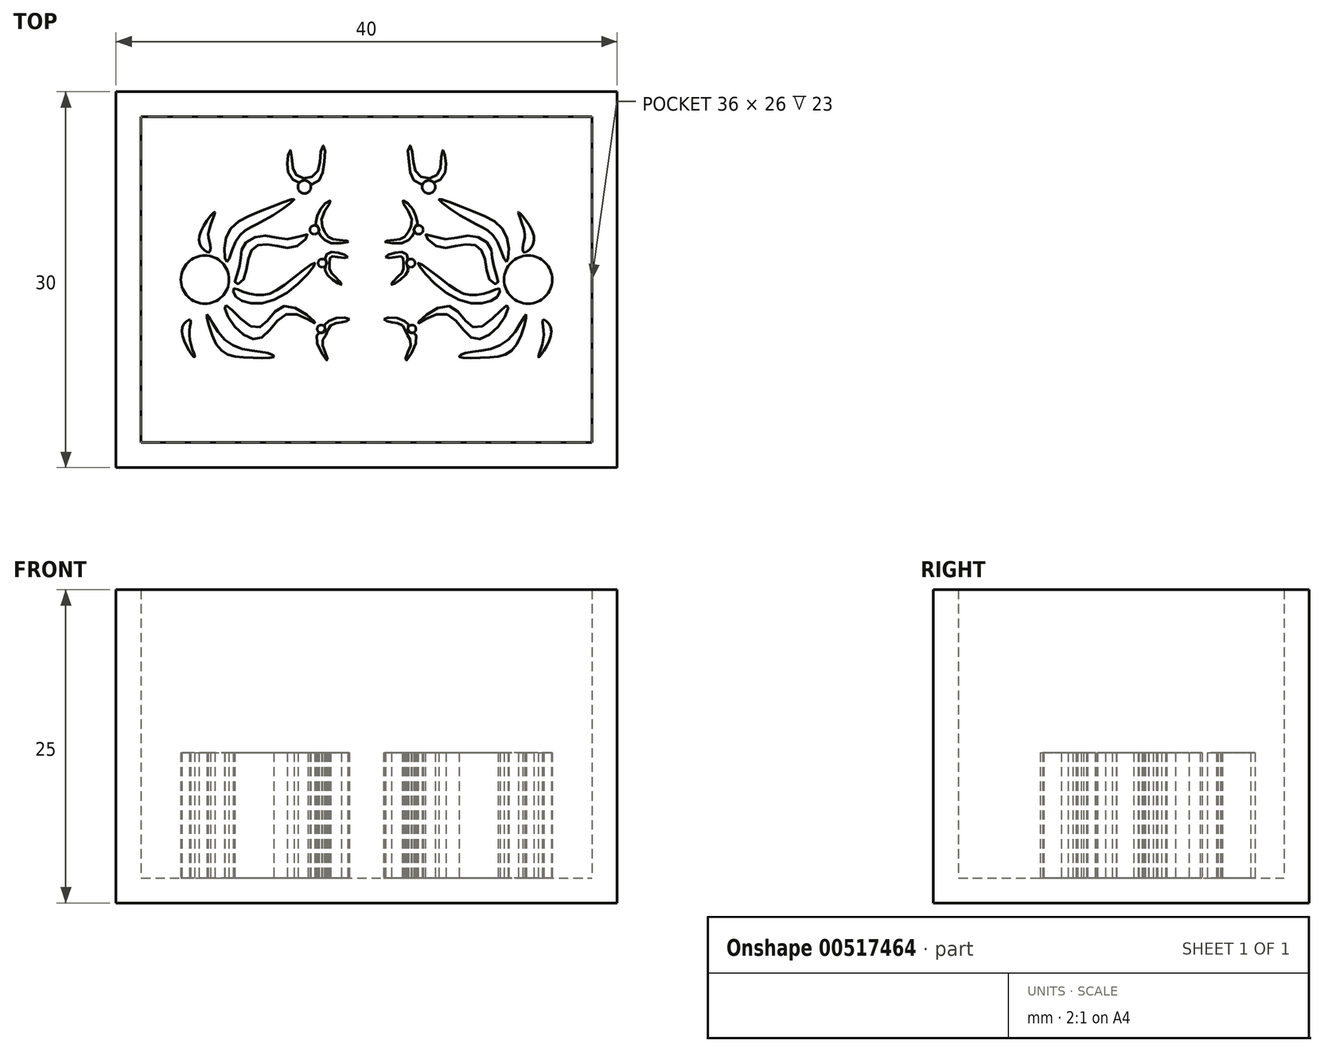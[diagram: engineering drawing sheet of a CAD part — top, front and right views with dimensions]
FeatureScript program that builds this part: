
annotation { "Feature Type Name" : "Feature", "Feature Type Description" : "" }
export const myFeature = defineFeature(function(context is Context, id is Id, definition is map)
    precondition{}
    {
        {
            var Q0;
            Q0=qCreatedBy(makeId("Top.planeOp"),FACE);
            var sketch = newSketch(context, id + "F0", { "sketchPlane" : qUnion([Q0])});
            skLineSegment(sketch, "E0.bottom", {"start": v(0, 0) * mm, "end": v(40, 0) * mm});
            skLineSegment(sketch, "E0.top", {"start": v(0, 30) * mm, "end": v(40, 30) * mm});
            skLineSegment(sketch, "E0.left", {"start": v(0, 0) * mm, "end": v(0, 30) * mm});
            skLineSegment(sketch, "E0.right", {"start": v(40, 0) * mm, "end": v(40, 30) * mm});
            skSolve(sketch);
        }
        {
            var Q0;
            Q0=makeQuery(id+"F0.imprint","IMPRINT",FACE,{"disambiguationData":[TD([[makeQuery(id+"F0.imprint","IMPRINT",EDGE,{"derivedFrom":sQuery(id+"F0.wireOp",EDGE,"E0.bottom")}),1.0]])]});
            extrude(context, id + "F1", {"entities" : qUnion([Q0]), "depth" : 25 * mm, "offsetDistance" : 25 * mm});
        }
        {
            var Q0;
            Q0=makeQuery(id+"F1.opExtrude","CAP_FACE",FACE,{"disambiguationData":[OSD([sQuery(id+"F0.wireOp",EDGE,"E0.bottom"),sQuery(id+"F0.wireOp",EDGE,"E0.top"),sQuery(id+"F0.wireOp",EDGE,"E0.left"),sQuery(id+"F0.wireOp",EDGE,"E0.right")])],"isStart":false});
            shell(context, id + "F2", {"entities" : qUnion([Q0]), "thickness" : 2 * mm});
        }
        {
            var Q0;
            Q0=makeQuery(id+"F2.opShell","OFFSET_FACE",FACE,{"disambiguationData":[OSD([sQuery(id+"F0.wireOp",EDGE,"E0.bottom"),sQuery(id+"F0.wireOp",EDGE,"E0.top"),sQuery(id+"F0.wireOp",EDGE,"E0.left"),sQuery(id+"F0.wireOp",EDGE,"E0.right")])]});
            var sketch = newSketch(context, id + "F3", { "sketchPlane" : qUnion([Q0])});
            skCircle(sketch, "E1", {"center": v(33.06, 17.38) * mm, "radius": 1.17 * mm});
            skSolve(sketch);
        }
        {
            var Q0;
            Q0 = qSketchRegion(id + "F3", true);
            extrude(context, id + "F4", {"entities" : qUnion([Q0]), "depth" : 10 * mm, "offsetDistance" : 25 * mm});
        }
        {
            var Q0;
            Q0=makeQuery(id+"F2.opShell","OFFSET_FACE",FACE,{"disambiguationData":[OSD([sQuery(id+"F0.wireOp",EDGE,"E0.bottom"),sQuery(id+"F0.wireOp",EDGE,"E0.top"),sQuery(id+"F0.wireOp",EDGE,"E0.left"),sQuery(id+"F0.wireOp",EDGE,"E0.right")])]});
            var sketch = newSketch(context, id + "F5", { "sketchPlane" : qUnion([Q0])});
            skCircle(sketch, "E2", {"center": v(34.3, 13.82) * mm, "radius": 1.1 * mm});
            skSolve(sketch);
        }
        {
            var Q0;
            Q0=makeQuery(id+"F5.imprint","IMPRINT",FACE,{"disambiguationData":[TD([[makeQuery(id+"F5.imprint","IMPRINT",EDGE,{"derivedFrom":sQuery(id+"F5.wireOp",EDGE,"E2")}),1.0]])]});
            extrude(context, id + "F6", {"entities" : qUnion([Q0]), "depth" : 10 * mm, "offsetDistance" : 25 * mm});
        }
        {
            var Q0;
            Q0=makeQuery(id+"F2.opShell","OFFSET_FACE",FACE,{"disambiguationData":[OSD([sQuery(id+"F0.wireOp",EDGE,"E0.bottom"),sQuery(id+"F0.wireOp",EDGE,"E0.top"),sQuery(id+"F0.wireOp",EDGE,"E0.left"),sQuery(id+"F0.wireOp",EDGE,"E0.right")])]});
            var sketch = newSketch(context, id + "F7", { "sketchPlane" : qUnion([Q0])});
            skCircle(sketch, "E3", {"center": v(21.96, 20.9) * mm, "radius": 2.86 * mm});
            skSolve(sketch);
        }
        {
            var Q0;
            Q0=makeQuery(id+"F7.imprint","IMPRINT",FACE,{"disambiguationData":[TD([[makeQuery(id+"F7.imprint","IMPRINT",EDGE,{"derivedFrom":sQuery(id+"F7.wireOp",EDGE,"E3")}),1.0]])]});
            extrude(context, id + "F8", {"entities" : qUnion([Q0]), "depth" : 25 * mm, "offsetDistance" : 25 * mm});
        }
        {
            var Q0;
            Q0=makeQuery(id+"F8.opExtrude","SWEPT_BODY",BODY,{"disambiguationData":[OSD([sQuery(id+"F7.wireOp",EDGE,"E3")])]});
            deleteBodies(context, id + "F9", {"entities" : qUnion([Q0])});
        }
        {
            var Q0;
            Q0=makeQuery(id+"F6.opExtrude","SWEPT_BODY",BODY,{"disambiguationData":[OSD([sQuery(id+"F5.wireOp",EDGE,"E2")])]});
            deleteBodies(context, id + "F10", {"entities" : qUnion([Q0])});
        }
        {
            var Q0;
            Q0=makeQuery(id+"F4.opExtrude","SWEPT_BODY",BODY,{"disambiguationData":[OSD([sQuery(id+"F3.wireOp",EDGE,"E1")])]});
            deleteBodies(context, id + "F11", {"entities" : qUnion([Q0])});
        }
        {
            var Q0;
            Q0=makeQuery(id+"F2.opShell","OFFSET_FACE",FACE,{"disambiguationData":[OSD([sQuery(id+"F0.wireOp",EDGE,"E0.bottom"),sQuery(id+"F0.wireOp",EDGE,"E0.top"),sQuery(id+"F0.wireOp",EDGE,"E0.left"),sQuery(id+"F0.wireOp",EDGE,"E0.right")])]});
            var sketch = newSketch(context, id + "F12", { "sketchPlane" : qUnion([Q0])});
            skCircle(sketch, "E4", {"center": v(32.9, 15) * mm, "radius": 1.92 * mm});
            skSolve(sketch);
        }
        {
            var Q0;
            Q0 = qSketchRegion(id + "F12", true);
            extrude(context, id + "F13", {"entities" : qUnion([Q0]), "depth" : 10 * mm, "offsetDistance" : 25 * mm});
        }
        {
            var Q0;
            Q0=qCreatedBy(makeId("Top.planeOp"),FACE);
            var sketch = newSketch(context, id + "F14", { "sketchPlane" : qUnion([Q0])});
            skCircle(sketch, "E5", {"center": v(32.77, 15.76) * mm, "radius": 0.71 * mm});
            skSolve(sketch);
        }
        {
            var Q0;
            Q0=sQuery(id+"F14.wireOp",EDGE,"E5");
            extrude(context, id + "F15", {"bodyType" : ToolBodyType.SURFACE, "surfaceEntities" : qUnion([Q0]), "depth" : 13 * mm, "offsetDistance" : 25 * mm});
        }
        {
            var Q0;
            Q0=qCreatedBy(makeId("Top.planeOp"),FACE);
            var sketch = newSketch(context, id + "F16", { "sketchPlane" : qUnion([Q0])});
            skCircle(sketch, "E6", {"center": v(33.33, 13.88) * mm, "radius": 0.58 * mm});
            skSolve(sketch);
        }
        {
            var Q0;
            Q0 = qSketchRegion(id + "F16", true);
            var Q1;
            Q1=sQuery(id+"F16.wireOp",EDGE,"E6");
            extrude(context, id + "F17", {"entities" : qUnion([Q0]), "bodyType" : ToolBodyType.SURFACE, "surfaceEntities" : qUnion([Q1]), "depth" : 13 * mm, "offsetDistance" : 25 * mm});
        }
        {
            var Q0;
            Q0=makeQuery(id+"F12.imprint","IMPRINT",FACE,{"disambiguationData":[TD([[makeQuery(id+"F12.imprint","IMPRINT",EDGE,{"derivedFrom":sQuery(id+"F12.wireOp",EDGE,"E4")}),-1.0]])]});
            var sketch = newSketch(context, id + "F18", { "sketchPlane" : qUnion([Q0])});
            skFitSpline(sketch, "E7", {"points": [v(31.16, 16.41) * mm, v(31.16, 18.52) * mm, v(28.04, 20.64) * mm, v(25.77, 21.42) * mm, v(27.7, 20) * mm, v(29.4, 19.1) * mm, v(30.5, 17.93) * mm, v(31.16, 16.41) * mm]});
            skSolve(sketch);
        }
        {
            var Q0;
            Q0 = qSketchRegion(id + "F18", true);
            extrude(context, id + "F19", {"entities" : qUnion([Q0]), "depth" : 10 * mm, "offsetDistance" : 25 * mm});
        }
        {
            var Q0;
            Q0=makeQuery(id+"F12.imprint","IMPRINT",FACE,{"disambiguationData":[TD([[makeQuery(id+"F12.imprint","IMPRINT",EDGE,{"derivedFrom":sQuery(id+"F12.wireOp",EDGE,"E4")}),-1.0]])]});
            var sketch = newSketch(context, id + "F20", { "sketchPlane" : qUnion([Q0])});
            skFitSpline(sketch, "E8", {"points": [v(33.17, 17.6) * mm, v(33.22, 18.88) * mm, v(32.12, 20.4) * mm, v(32.6, 18.84) * mm, v(32.48, 17.79) * mm, v(32.56, 17.17) * mm, v(33.17, 17.6) * mm]});
            skSolve(sketch);
        }
        {
            var Q0;
            Q0 = qSketchRegion(id + "F20", true);
            extrude(context, id + "F21", {"entities" : qUnion([Q0]), "depth" : 10 * mm, "offsetDistance" : 25 * mm});
        }
        {
            var Q0;
            Q0=makeQuery(id+"F12.imprint","IMPRINT",FACE,{"disambiguationData":[TD([[makeQuery(id+"F12.imprint","IMPRINT",EDGE,{"derivedFrom":sQuery(id+"F12.wireOp",EDGE,"E4")}),-1.0]])]});
            var sketch = newSketch(context, id + "F22", { "sketchPlane" : qUnion([Q0])});
            skFitSpline(sketch, "E9", {"points": [v(30.34, 15.44) * mm, v(30.04, 16.6) * mm, v(29.83, 17.7) * mm, v(28.31, 18.52) * mm, v(26.22, 18.24) * mm, v(24.69, 18.58) * mm, v(25.56, 17.68) * mm, v(27.24, 17.7) * mm, v(28.82, 17.68) * mm, v(29.46, 16.56) * mm, v(29.92, 14.87) * mm, v(30.47, 14.67) * mm, v(30.34, 15.44) * mm]});
            skSolve(sketch);
        }
        {
            var Q0;
            Q0 = qSketchRegion(id + "F22", true);
            extrude(context, id + "F23", {"entities" : qUnion([Q0]), "depth" : 10 * mm, "offsetDistance" : 25 * mm});
        }
        {
            var Q0;
            Q0=makeQuery(id+"F12.imprint","IMPRINT",FACE,{"disambiguationData":[TD([[makeQuery(id+"F12.imprint","IMPRINT",EDGE,{"derivedFrom":sQuery(id+"F12.wireOp",EDGE,"E4")}),-1.0]])]});
            var sketch = newSketch(context, id + "F24", { "sketchPlane" : qUnion([Q0])});
            skFitSpline(sketch, "E10", {"points": [v(30.43, 13.64) * mm, v(27.12, 13.5) * mm, v(24.13, 16.34) * mm, v(26.55, 14.6) * mm, v(28.42, 13.76) * mm, v(30.03, 14.1) * mm, v(30.6, 14.26) * mm, v(30.43, 13.64) * mm]});
            skSolve(sketch);
        }
        {
            var Q0;
            Q0 = qSketchRegion(id + "F24", true);
            extrude(context, id + "F25", {"entities" : qUnion([Q0]), "depth" : 10 * mm, "offsetDistance" : 25 * mm});
        }
        {
            var Q0;
            Q0=makeQuery(id+"F12.imprint","IMPRINT",FACE,{"disambiguationData":[TD([[makeQuery(id+"F12.imprint","IMPRINT",EDGE,{"derivedFrom":sQuery(id+"F12.wireOp",EDGE,"E4")}),-1.0]])]});
            var sketch = newSketch(context, id + "F26", { "sketchPlane" : qUnion([Q0])});
            skFitSpline(sketch, "E11", {"points": [v(31.2, 12.96) * mm, v(28.78, 11.15) * mm, v(26.48, 12.9) * mm, v(24.07, 11.51) * mm, v(26.19, 12.3) * mm, v(28.6, 10.27) * mm, v(31.02, 12) * mm, v(31.2, 12.96) * mm]});
            skSolve(sketch);
        }
        {
            var Q0;
            Q0 = qSketchRegion(id + "F26", true);
            extrude(context, id + "F27", {"entities" : qUnion([Q0]), "depth" : 10 * mm, "offsetDistance" : 25 * mm});
        }
        {
            var Q0;
            Q0=makeQuery(id+"F12.imprint","IMPRINT",FACE,{"disambiguationData":[TD([[makeQuery(id+"F12.imprint","IMPRINT",EDGE,{"derivedFrom":sQuery(id+"F12.wireOp",EDGE,"E4")}),-1.0]])]});
            var sketch = newSketch(context, id + "F28", { "sketchPlane" : qUnion([Q0])});
            skFitSpline(sketch, "E12", {"points": [v(32.73, 12.23) * mm, v(31.2, 10.1) * mm, v(27.93, 9.15) * mm, v(27.4, 8.85) * mm, v(29.68, 8.8) * mm, v(31.94, 9.76) * mm, v(32.73, 12.23) * mm]});
            skSolve(sketch);
        }
        {
            var Q0;
            Q0 = qSketchRegion(id + "F28", true);
            extrude(context, id + "F29", {"entities" : qUnion([Q0]), "depth" : 10 * mm, "offsetDistance" : 25 * mm});
        }
        {
            var Q0;
            Q0=makeQuery(id+"F12.imprint","IMPRINT",FACE,{"disambiguationData":[TD([[makeQuery(id+"F12.imprint","IMPRINT",EDGE,{"derivedFrom":sQuery(id+"F12.wireOp",EDGE,"E4")}),-1.0]])]});
            var sketch = newSketch(context, id + "F30", { "sketchPlane" : qUnion([Q0])});
            skFitSpline(sketch, "E13", {"points": [v(34.08, 11.79) * mm, v(34.75, 11) * mm, v(33.74, 8.83) * mm, v(34.14, 10.5) * mm, v(34.08, 11.79) * mm]});
            skSolve(sketch);
        }
        {
            var Q0;
            Q0 = qSketchRegion(id + "F30", true);
            extrude(context, id + "F31", {"entities" : qUnion([Q0]), "depth" : 10 * mm, "offsetDistance" : 25 * mm});
        }
        {
            var Q0;
            Q0=qCreatedBy(makeId("Right.planeOp"),FACE);
            cPlane(context, id + "F32", {"entities" : qUnion([Q0]), "cplaneType" : CPlaneType.OFFSET, "offset" : 20 * mm, "width" : 150 * mm, "height" : 150 * mm});
        }
        {
            var Q0;
            Q0=makeQuery(id+"F12.imprint","IMPRINT",FACE,{"disambiguationData":[TD([[makeQuery(id+"F12.imprint","IMPRINT",EDGE,{"derivedFrom":sQuery(id+"F12.wireOp",EDGE,"E4")}),-1.0]])]});
            var sketch = newSketch(context, id + "F33", { "sketchPlane" : qUnion([Q0])});
            skCircle(sketch, "E14", {"center": v(25.04, 22.1) * mm, "radius": 0.48 * mm});
            skFitSpline(sketch, "E15", {"points": [v(24.78, 21.7) * mm, v(24.43, 20.97) * mm, v(22.2, 21.2) * mm, v(21.84, 21.56) * mm, v(22.86, 21.49) * mm, v(23.88, 21.52) * mm, v(24.03, 22.1) * mm, v(24.25, 22.94) * mm, v(23.92, 23.98) * mm, v(23.94, 24.53) * mm, v(24.5, 24.08) * mm, v(25.04, 22.58) * mm], "startDerivative": vector(-1.18, -10.43) * mm, "endDerivative": vector(3.27, -13.82) * mm});
            skSolve(sketch);
        }
        {
            var Q0;
            Q0 = qSketchRegion(id + "F33", true);
            extrude(context, id + "F34", {"entities" : qUnion([Q0]), "depth" : 10 * mm, "offsetDistance" : 25 * mm});
        }
        {
            var Q0;
            Q0=makeQuery(id+"F12.imprint","IMPRINT",FACE,{"disambiguationData":[TD([[makeQuery(id+"F12.imprint","IMPRINT",EDGE,{"derivedFrom":sQuery(id+"F12.wireOp",EDGE,"E4")}),-1.0]])]});
            var sketch = newSketch(context, id + "F35", { "sketchPlane" : qUnion([Q0])});
            skCircle(sketch, "E16", {"center": v(23.7, 18.69) * mm, "radius": 0.52 * mm});
            skFitSpline(sketch, "E17", {"points": [v(23.7, 18.17) * mm, v(22.99, 17.37) * mm, v(21.27, 16.99) * mm, v(22.58, 17.78) * mm, v(22.88, 18.1) * mm, v(22.76, 18.69) * mm, v(22.73, 19.4) * mm, v(22.13, 20.23) * mm, v(22, 20.54) * mm, v(22.5, 20.52) * mm, v(23.14, 19.83) * mm, v(23.2, 19.49) * mm, v(23.34, 19.05) * mm], "startDerivative": vector(-4, -8.51) * mm, "endDerivative": vector(2.63, -7.06) * mm});
            skSolve(sketch);
        }
        {
            var Q0;
            Q0 = qSketchRegion(id + "F35", true);
            extrude(context, id + "F36", {"entities" : qUnion([Q0]), "depth" : 10 * mm, "offsetDistance" : 25 * mm});
        }
        {
            var Q0;
            Q0=makeQuery(id+"F12.imprint","IMPRINT",FACE,{"disambiguationData":[TD([[makeQuery(id+"F12.imprint","IMPRINT",EDGE,{"derivedFrom":sQuery(id+"F12.wireOp",EDGE,"E4")}),-1.0]])]});
            var sketch = newSketch(context, id + "F37", { "sketchPlane" : qUnion([Q0])});
            skCircle(sketch, "E18", {"center": v(23.12, 15.63) * mm, "radius": 0.5 * mm});
            skFitSpline(sketch, "E19", {"points": [v(22.97, 16.1) * mm, v(22.2, 16.43) * mm, v(20.6, 16.07) * mm, v(20.43, 15.68) * mm, v(21.42, 15.94) * mm, v(22.63, 15.73) * mm, v(22.28, 14.57) * mm, v(21.91, 13.4) * mm, v(22.77, 14.04) * mm, v(23.12, 15.13) * mm], "startDerivative": vector(-6.4, 4.26) * mm, "endDerivative": vector(1.17, 9.37) * mm});
            skSolve(sketch);
        }
        {
            var Q0;
            Q0 = qSketchRegion(id + "F37", true);
            extrude(context, id + "F38", {"entities" : qUnion([Q0]), "depth" : 10 * mm, "offsetDistance" : 25 * mm});
        }
        {
            var Q0;
            Q0=makeQuery(id+"F12.imprint","IMPRINT",FACE,{"disambiguationData":[TD([[makeQuery(id+"F12.imprint","IMPRINT",EDGE,{"derivedFrom":sQuery(id+"F12.wireOp",EDGE,"E4")}),-1.0]])]});
            var sketch = newSketch(context, id + "F39", { "sketchPlane" : qUnion([Q0])});
            skCircle(sketch, "E20", {"center": v(23.48, 10.89) * mm, "radius": 0.36 * mm});
            skFitSpline(sketch, "E21", {"points": [v(23.8, 10.7) * mm, v(24.59, 9.36) * mm, v(23.9, 7.91) * mm, v(24.05, 8.75) * mm, v(24.07, 9.56) * mm, v(23.4, 10.23) * mm, v(22.57, 10.68) * mm, v(21.36, 10.65) * mm, v(20.96, 10.76) * mm, v(21.98, 11.04) * mm, v(23.13, 10.99) * mm], "startDerivative": vector(10.24, -8.94) * mm, "endDerivative": vector(9.79, -1.38) * mm});
            skSolve(sketch);
        }
        {
            var Q0;
            Q0 = qSketchRegion(id + "F39", true);
            extrude(context, id + "F40", {"entities" : qUnion([Q0]), "depth" : 10 * mm, "offsetDistance" : 25 * mm});
        }
        {
            var Q0;
            Q0=makeQuery(id+"F34.opExtrude","SWEPT_BODY",BODY,{"disambiguationData":[OSD([sQuery(id+"F33.wireOp",EDGE,"E14"),sQuery(id+"F33.wireOp",EDGE,"E15")])]});
            deleteBodies(context, id + "F41", {"entities" : qUnion([Q0])});
        }
        {
            var Q0;
            Q0=makeQuery(id+"F12.imprint","IMPRINT",FACE,{"disambiguationData":[TD([[makeQuery(id+"F12.imprint","IMPRINT",EDGE,{"derivedFrom":sQuery(id+"F12.wireOp",EDGE,"E4")}),-1.0]])]});
            var sketch = newSketch(context, id + "F42", { "sketchPlane" : qUnion([Q0])});
            skCircle(sketch, "E22", {"center": v(24.96, 22.4) * mm, "radius": 0.52 * mm});
            skSolve(sketch);
        }
        {
            var Q0;
            Q0 = qSketchRegion(id + "F42", true);
            extrude(context, id + "F43", {"entities" : qUnion([Q0]), "depth" : 10 * mm, "offsetDistance" : 25 * mm});
        }
        {
            var Q0;
            Q0=makeQuery(id+"F42.imprint","IMPRINT",FACE,{"disambiguationData":[TD([[makeQuery(id+"F42.imprint","IMPRINT",EDGE,{"derivedFrom":sQuery(id+"F42.wireOp",EDGE,"E22")}),-1.0]])]});
            var sketch = newSketch(context, id + "F44", { "sketchPlane" : qUnion([Q0])});
            skFitSpline(sketch, "E23", {"points": [v(25.37, 22.74) * mm, v(26.07, 23.17) * mm, v(26.34, 24.1) * mm, v(26.22, 25.08) * mm, v(26.07, 25.33) * mm, v(25.94, 24.28) * mm, v(25.63, 23.36) * mm, v(24.72, 23.09) * mm, v(23.93, 23.63) * mm, v(23.7, 24.8) * mm, v(23.5, 25.69) * mm, v(23.34, 25.56) * mm, v(23.42, 24.1) * mm, v(23.74, 22.96) * mm, v(24.46, 22.6) * mm, v(24.5, 22.66) * mm, v(24.62, 22.8) * mm, v(24.8, 22.91) * mm, v(25.01, 22.94) * mm, v(25.22, 22.88) * mm, v(25.37, 22.74) * mm]});
            skSolve(sketch);
        }
        {
            var Q0;
            Q0 = qSketchRegion(id + "F44", true);
            extrude(context, id + "F45", {"entities" : qUnion([Q0]), "depth" : 10 * mm, "offsetDistance" : 25 * mm});
        }
        {
            var Q0;
            Q0=makeQuery(id+"F36.opExtrude","SWEPT_BODY",BODY,{"disambiguationData":[OSD([sQuery(id+"F35.wireOp",EDGE,"E16"),sQuery(id+"F35.wireOp",EDGE,"E17")])]});
            deleteBodies(context, id + "F46", {"entities" : qUnion([Q0])});
        }
        {
            var Q0;
            Q0=makeQuery(id+"F12.imprint","IMPRINT",FACE,{"disambiguationData":[TD([[makeQuery(id+"F12.imprint","IMPRINT",EDGE,{"derivedFrom":sQuery(id+"F12.wireOp",EDGE,"E4")}),-1.0]])]});
            var sketch = newSketch(context, id + "F47", { "sketchPlane" : qUnion([Q0])});
            skCircle(sketch, "E24", {"center": v(24.17, 18.98) * mm, "radius": 0.35 * mm});
            skSolve(sketch);
        }
        {
            var Q0;
            Q0 = qSketchRegion(id + "F47", true);
            extrude(context, id + "F48", {"entities" : qUnion([Q0]), "depth" : 10 * mm, "offsetDistance" : 25 * mm});
        }
        {
            var Q0;
            Q0=makeQuery(id+"F12.imprint","IMPRINT",FACE,{"disambiguationData":[TD([[makeQuery(id+"F12.imprint","IMPRINT",EDGE,{"derivedFrom":sQuery(id+"F12.wireOp",EDGE,"E4")}),-1.0]])]});
            var sketch = newSketch(context, id + "F49", { "sketchPlane" : qUnion([Q0])});
            skFitSpline(sketch, "E25", {"points": [v(23.82, 18.85) * mm, v(23.8, 19.02) * mm, v(23.86, 19.18) * mm, v(24.02, 19.31) * mm, v(24.22, 19.34) * mm, v(24.58, 19.5) * mm, v(24.83, 20.22) * mm, v(24.83, 20.8) * mm, v(24.74, 21.12) * mm, v(24.6, 20.81) * mm, v(24.49, 20) * mm, v(24.02, 19.63) * mm, v(23.18, 19.78) * mm, v(22.71, 20.6) * mm, v(22.59, 20.88) * mm, v(22.5, 20.72) * mm, v(22.81, 19.85) * mm, v(23.39, 19.17) * mm, v(23.6, 19.04) * mm, v(23.82, 18.85) * mm]});
            skSolve(sketch);
        }
        {
            var Q0;
            Q0 = qSketchRegion(id + "F49", true);
            extrude(context, id + "F50", {"entities" : qUnion([Q0]), "depth" : 10 * mm, "offsetDistance" : 25 * mm});
        }
        {
            var Q0;
            Q0=makeQuery(id+"F50.opExtrude","SWEPT_BODY",BODY,{"disambiguationData":[OSD([sQuery(id+"F49.wireOp",EDGE,"E25")])]});
            deleteBodies(context, id + "F51", {"entities" : qUnion([Q0])});
        }
        {
            var Q0;
            Q0=makeQuery(id+"F42.imprint","IMPRINT",FACE,{"disambiguationData":[TD([[makeQuery(id+"F42.imprint","IMPRINT",EDGE,{"derivedFrom":sQuery(id+"F42.wireOp",EDGE,"E22")}),-1.0]])]});
            var sketch = newSketch(context, id + "F52", { "sketchPlane" : qUnion([Q0])});
            skFitSpline(sketch, "E26", {"points": [v(24.04, 19.34) * mm, v(24.27, 19.37) * mm, v(24.84, 19.6) * mm, v(24.76, 20.82) * mm, v(24.42, 21.37) * mm, v(24.58, 20.37) * mm, v(24.59, 19.9) * mm, v(23.82, 19.7) * mm, v(22.97, 20.08) * mm, v(22.37, 20.98) * mm, v(22, 20.98) * mm, v(22.74, 19.95) * mm, v(23.42, 19.37) * mm, v(23.8, 19.22) * mm, v(24.04, 19.34) * mm]});
            skSolve(sketch);
        }
        {
            var Q0;
            Q0 = qSketchRegion(id + "F52", true);
            extrude(context, id + "F53", {"entities" : qUnion([Q0]), "depth" : 10 * mm, "offsetDistance" : 25 * mm});
        }
        {
            var Q0;
            Q0=makeQuery(id+"F38.opExtrude","SWEPT_BODY",BODY,{"disambiguationData":[OSD([sQuery(id+"F37.wireOp",EDGE,"E18"),sQuery(id+"F37.wireOp",EDGE,"E19")])]});
            deleteBodies(context, id + "F54", {"entities" : qUnion([Q0])});
        }
        {
            var Q0;
            Q0=makeQuery(id+"F53.opExtrude","SWEPT_BODY",BODY,{"disambiguationData":[OSD([sQuery(id+"F52.wireOp",EDGE,"E26")])]});
            deleteBodies(context, id + "F55", {"entities" : qUnion([Q0])});
        }
        {
            var Q0;
            Q0=makeQuery(id+"F12.imprint","IMPRINT",FACE,{"disambiguationData":[TD([[makeQuery(id+"F12.imprint","IMPRINT",EDGE,{"derivedFrom":sQuery(id+"F12.wireOp",EDGE,"E4")}),-1.0]])]});
            var sketch = newSketch(context, id + "F56", { "sketchPlane" : qUnion([Q0])});
            skFitSpline(sketch, "E27", {"points": [v(23.78, 19) * mm, v(23.81, 18.8) * mm, v(23.65, 18.49) * mm, v(22.87, 17.94) * mm, v(21.44, 18.03) * mm, v(22.03, 18.16) * mm, v(22.92, 18.33) * mm, v(23.4, 18.92) * mm, v(23.54, 20.06) * mm, v(22.85, 21.28) * mm, v(23.4, 21.01) * mm, v(24, 19.86) * mm, v(24.08, 19.4) * mm, v(24.05, 19.35) * mm, v(23.93, 19.29) * mm, v(23.78, 19) * mm]});
            skSolve(sketch);
        }
        {
            var Q0;
            Q0 = qSketchRegion(id + "F56", true);
            extrude(context, id + "F57", {"entities" : qUnion([Q0]), "depth" : 10 * mm, "offsetDistance" : 25 * mm});
        }
        {
            var Q0;
            Q0=makeQuery(id+"F40.opExtrude","SWEPT_BODY",BODY,{"disambiguationData":[OSD([sQuery(id+"F39.wireOp",EDGE,"E20"),sQuery(id+"F39.wireOp",EDGE,"E21")])]});
            deleteBodies(context, id + "F58", {"entities" : qUnion([Q0])});
        }
        {
            var Q0;
            Q0=makeQuery(id+"F12.imprint","IMPRINT",FACE,{"disambiguationData":[TD([[makeQuery(id+"F12.imprint","IMPRINT",EDGE,{"derivedFrom":sQuery(id+"F12.wireOp",EDGE,"E4")}),-1.0]])]});
            var sketch = newSketch(context, id + "F59", { "sketchPlane" : qUnion([Q0])});
            skCircle(sketch, "E28", {"center": v(23.2, 15.86) * mm, "radius": 0.51 * mm});
            skSolve(sketch);
        }
        {
            var Q0;
            Q0 = qSketchRegion(id + "F59", true);
            extrude(context, id + "F60", {"entities" : qUnion([Q0]), "depth" : 10 * mm, "offsetDistance" : 25 * mm});
        }
        {
            var Q0;
            Q0=makeQuery(id+"F60.opExtrude","SWEPT_BODY",BODY,{"disambiguationData":[OSD([sQuery(id+"F59.wireOp",EDGE,"E28")])]});
            deleteBodies(context, id + "F61", {"entities" : qUnion([Q0])});
        }
        {
            var Q0;
            Q0=makeQuery(id+"F12.imprint","IMPRINT",FACE,{"disambiguationData":[TD([[makeQuery(id+"F12.imprint","IMPRINT",EDGE,{"derivedFrom":sQuery(id+"F12.wireOp",EDGE,"E4")}),-1.0]])]});
            var sketch = newSketch(context, id + "F62", { "sketchPlane" : qUnion([Q0])});
            skCircle(sketch, "E29", {"center": v(23.54, 16.32) * mm, "radius": 0.33 * mm});
            skSolve(sketch);
        }
        {
            var Q0;
            Q0 = qSketchRegion(id + "F62", true);
            extrude(context, id + "F63", {"entities" : qUnion([Q0]), "depth" : 10 * mm, "offsetDistance" : 25 * mm});
        }
        {
            var Q0;
            Q0=makeQuery(id+"F12.imprint","IMPRINT",FACE,{"disambiguationData":[TD([[makeQuery(id+"F12.imprint","IMPRINT",EDGE,{"derivedFrom":sQuery(id+"F12.wireOp",EDGE,"E4")}),-1.0]])]});
            var sketch = newSketch(context, id + "F64", { "sketchPlane" : qUnion([Q0])});
            skCircle(sketch, "E30", {"center": v(23.62, 11.06) * mm, "radius": 0.32 * mm});
            skSolve(sketch);
        }
        {
            var Q0;
            Q0 = qSketchRegion(id + "F64", true);
            extrude(context, id + "F65", {"entities" : qUnion([Q0]), "depth" : 10 * mm, "offsetDistance" : 25 * mm});
        }
        {
            var Q0;
            Q0=makeQuery(id+"F12.imprint","IMPRINT",FACE,{"disambiguationData":[TD([[makeQuery(id+"F12.imprint","IMPRINT",EDGE,{"derivedFrom":sQuery(id+"F12.wireOp",EDGE,"E4")}),-1.0]])]});
            var sketch = newSketch(context, id + "F66", { "sketchPlane" : qUnion([Q0])});
            skFitSpline(sketch, "E31", {"points": [v(21.51, 16.8) * mm, v(22.1, 17.12) * mm, v(23.13, 17.09) * mm, v(23.3, 16.6) * mm, v(23.23, 16.5) * mm, v(23.17, 16.35) * mm, v(23.27, 16.09) * mm, v(23.26, 15.6) * mm, v(22.41, 14.8) * mm, v(22, 14.6) * mm, v(22.45, 15.2) * mm, v(22.92, 15.73) * mm, v(22.93, 16.54) * mm, v(22.85, 16.84) * mm, v(22.07, 16.76) * mm, v(21.51, 16.8) * mm]});
            skSolve(sketch);
        }
        {
            var Q0;
            Q0 = qSketchRegion(id + "F66", true);
            extrude(context, id + "F67", {"entities" : qUnion([Q0]), "depth" : 10 * mm, "offsetDistance" : 25 * mm});
        }
        {
            var Q0;
            Q0=makeQuery(id+"F12.imprint","IMPRINT",FACE,{"disambiguationData":[TD([[makeQuery(id+"F12.imprint","IMPRINT",EDGE,{"derivedFrom":sQuery(id+"F12.wireOp",EDGE,"E4")}),-1.0]])]});
            var sketch = newSketch(context, id + "F68", { "sketchPlane" : qUnion([Q0])});
            skFitSpline(sketch, "E32", {"points": [v(20.93, 12.03) * mm, v(22.3, 12.53) * mm, v(23.25, 12.58) * mm, v(23.52, 11.6) * mm, v(23.33, 11.34) * mm, v(23.28, 11.08) * mm, v(23.4, 10.79) * mm, v(23.7, 10.74) * mm, v(24.08, 10.05) * mm, v(23.08, 8.19) * mm, v(23.2, 9.06) * mm, v(23.36, 9.96) * mm, v(22.9, 11.07) * mm, v(22.73, 11.88) * mm, v(21.63, 11.7) * mm, v(20.93, 12.03) * mm]});
            skSolve(sketch);
        }
        {
            var Q0;
            Q0 = qSketchRegion(id + "F68", true);
            extrude(context, id + "F69", {"entities" : qUnion([Q0]), "depth" : 10 * mm, "offsetDistance" : 25 * mm});
        }
        {
            var Q0;
            Q0=makeQuery(id+"F69.opExtrude","SWEPT_BODY",BODY,{"disambiguationData":[OSD([sQuery(id+"F68.wireOp",EDGE,"E32")])]});
            deleteBodies(context, id + "F70", {"entities" : qUnion([Q0])});
        }
        {
            var Q0;
            Q0=makeQuery(id+"F12.imprint","IMPRINT",FACE,{"disambiguationData":[TD([[makeQuery(id+"F12.imprint","IMPRINT",EDGE,{"derivedFrom":sQuery(id+"F12.wireOp",EDGE,"E4")}),-1.0]])]});
            var sketch = newSketch(context, id + "F71", { "sketchPlane" : qUnion([Q0])});
            skFitSpline(sketch, "E33", {"points": [v(21.37, 11.85) * mm, v(22.35, 11.95) * mm, v(23.33, 11.44) * mm, v(23.36, 11.3) * mm, v(23.31, 11.2) * mm, v(23.3, 10.98) * mm, v(23.5, 10.76) * mm, v(23.8, 10.76) * mm, v(23.98, 10.09) * mm, v(23.12, 8.52) * mm, v(23.21, 9) * mm, v(23.54, 10.01) * mm, v(23.2, 10.68) * mm, v(22.94, 11.28) * mm, v(22.28, 11.58) * mm, v(21.61, 11.67) * mm, v(21.37, 11.85) * mm]});
            skSolve(sketch);
        }
        {
            var Q0;
            Q0 = qSketchRegion(id + "F71", true);
            extrude(context, id + "F72", {"entities" : qUnion([Q0]), "depth" : 10 * mm, "offsetDistance" : 25 * mm});
        }
        {
            var Q0;
            Q0=makeQuery(id+"F13.opExtrude","SWEPT_BODY",BODY,{"disambiguationData":[OSD([sQuery(id+"F12.wireOp",EDGE,"E4")])]});
            var Q1;
            Q1=makeQuery(id+"F19.opExtrude","SWEPT_BODY",BODY,{"disambiguationData":[OSD([sQuery(id+"F18.wireOp",EDGE,"E7")])]});
            var Q2;
            Q2=makeQuery(id+"F21.opExtrude","SWEPT_BODY",BODY,{"disambiguationData":[OSD([sQuery(id+"F20.wireOp",EDGE,"E8")])]});
            var Q3;
            Q3=makeQuery(id+"F27.opExtrude","SWEPT_BODY",BODY,{"disambiguationData":[OSD([sQuery(id+"F26.wireOp",EDGE,"E11")])]});
            var Q4;
            Q4=makeQuery(id+"F29.opExtrude","SWEPT_BODY",BODY,{"disambiguationData":[OSD([sQuery(id+"F28.wireOp",EDGE,"E12")])]});
            var Q5;
            Q5=makeQuery(id+"F25.opExtrude","SWEPT_BODY",BODY,{"disambiguationData":[OSD([sQuery(id+"F24.wireOp",EDGE,"E10")])]});
            var Q6;
            Q6=makeQuery(id+"F23.opExtrude","SWEPT_BODY",BODY,{"disambiguationData":[OSD([sQuery(id+"F22.wireOp",EDGE,"E9")])]});
            var Q7;
            Q7=makeQuery(id+"F31.opExtrude","SWEPT_BODY",BODY,{"disambiguationData":[OSD([sQuery(id+"F30.wireOp",EDGE,"E13")])]});
            var Q8;
            Q8=makeQuery(id+"F43.opExtrude","SWEPT_BODY",BODY,{"disambiguationData":[OSD([sQuery(id+"F42.wireOp",EDGE,"E22")])]});
            var Q9;
            Q9=makeQuery(id+"F45.opExtrude","SWEPT_BODY",BODY,{"disambiguationData":[OSD([sQuery(id+"F44.wireOp",EDGE,"E23")])]});
            var Q10;
            Q10=makeQuery(id+"F48.opExtrude","SWEPT_BODY",BODY,{"disambiguationData":[OSD([sQuery(id+"F47.wireOp",EDGE,"E24")])]});
            var Q11;
            Q11=makeQuery(id+"F57.opExtrude","SWEPT_BODY",BODY,{"disambiguationData":[OSD([sQuery(id+"F56.wireOp",EDGE,"E27")])]});
            var Q12;
            Q12=makeQuery(id+"F63.opExtrude","SWEPT_BODY",BODY,{"disambiguationData":[OSD([sQuery(id+"F62.wireOp",EDGE,"E29")])]});
            var Q13;
            Q13=makeQuery(id+"F65.opExtrude","SWEPT_BODY",BODY,{"disambiguationData":[OSD([sQuery(id+"F64.wireOp",EDGE,"E30")])]});
            var Q14;
            Q14=makeQuery(id+"F67.opExtrude","SWEPT_BODY",BODY,{"disambiguationData":[OSD([sQuery(id+"F66.wireOp",EDGE,"E31")])]});
            var Q15;
            Q15=makeQuery(id+"F72.opExtrude","SWEPT_BODY",BODY,{"disambiguationData":[OSD([sQuery(id+"F71.wireOp",EDGE,"E33")])]});
            var Q16;
            Q16=makeQuery(id+"F15.opExtrude","SWEPT_BODY",BODY,{"disambiguationData":[OSD([sQuery(id+"F14.wireOp",EDGE,"E5")])]});
            var Q17;
            Q17=makeQuery(id+"F17.opExtrude","SWEPT_BODY",BODY,{"disambiguationData":[OSD([sQuery(id+"F16.wireOp",EDGE,"E6")])]});
            var Q18;
            Q18=qCreatedBy(id+"F32.planeOp",FACE);
            mirror(context, id + "F73", {"entities" : qUnion([Q0, Q1, Q2, Q3, Q4, Q5, Q6, Q7, Q8, Q9, Q10, Q11, Q12, Q13, Q14, Q15, Q16, Q17]), "mirrorPlane" : qUnion([Q18])});
        }
    });
